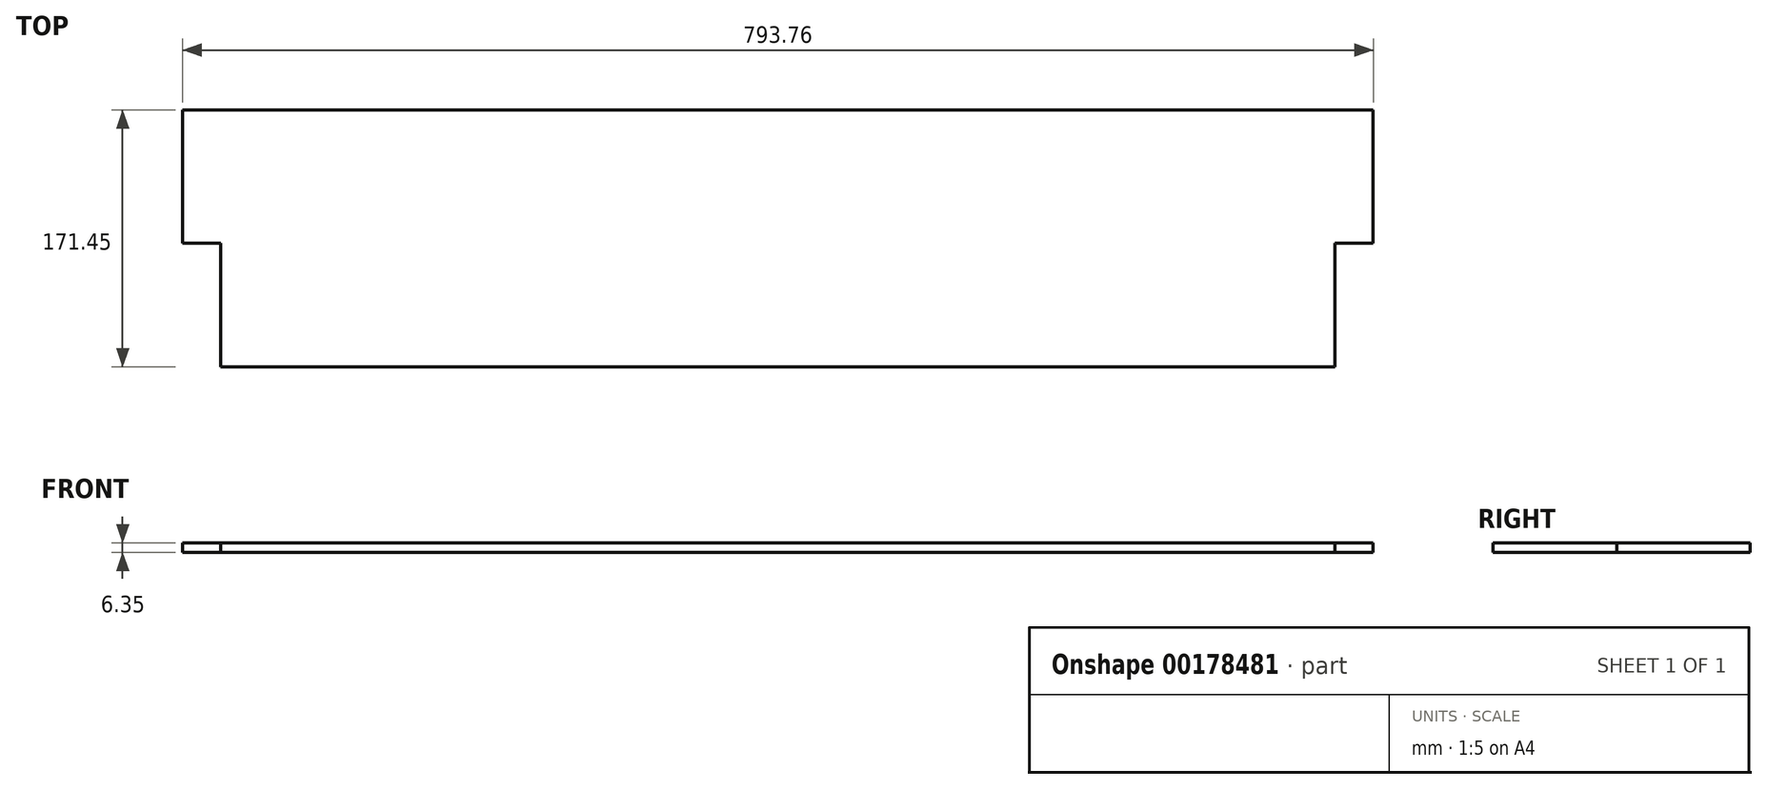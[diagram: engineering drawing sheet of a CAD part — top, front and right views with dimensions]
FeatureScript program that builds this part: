
annotation { "Feature Type Name" : "Feature", "Feature Type Description" : "" }
export const myFeature = defineFeature(function(context is Context, id is Id, definition is map)
    precondition{}
    {
        {
            var Q0;
            Q0=qCreatedBy(makeId("Top.planeOp"),FACE);
            var sketch = newSketch(context, id + "F0", { "sketchPlane" : qUnion([Q0])});
            skLineSegment(sketch, "E0.bottom", {"start": v(-396.88, 44.45) * mm, "end": v(396.88, 44.45) * mm});
            skLineSegment(sketch, "E0.top", {"start": v(-396.88, -44.45) * mm, "end": v(396.88, -44.45) * mm});
            skLineSegment(sketch, "E0.left", {"start": v(-396.88, 44.45) * mm, "end": v(-396.88, -44.45) * mm});
            skLineSegment(sketch, "E0.right", {"start": v(396.88, 44.45) * mm, "end": v(396.88, -44.45) * mm});
            skPoint(sketch, "E0.middle", {"position": v(0, 0) * mm});
            skLineSegment(sketch, "E1.bottom", {"start": v(-371.48, -44.45) * mm, "end": v(371.48, -44.45) * mm});
            skLineSegment(sketch, "E1.top", {"start": v(-371.48, -127) * mm, "end": v(371.48, -127) * mm});
            skLineSegment(sketch, "E1.left", {"start": v(-371.48, -44.45) * mm, "end": v(-371.48, -127) * mm});
            skLineSegment(sketch, "E1.right", {"start": v(371.48, -44.45) * mm, "end": v(371.48, -127) * mm});
            skSolve(sketch);
        }
        {
            var Q0;
            Q0 = qSketchRegion(id + "F0", true);
            extrude(context, id + "F1", {"entities" : qUnion([Q0]), "depth" : 6.35 * mm});
        }
    });
